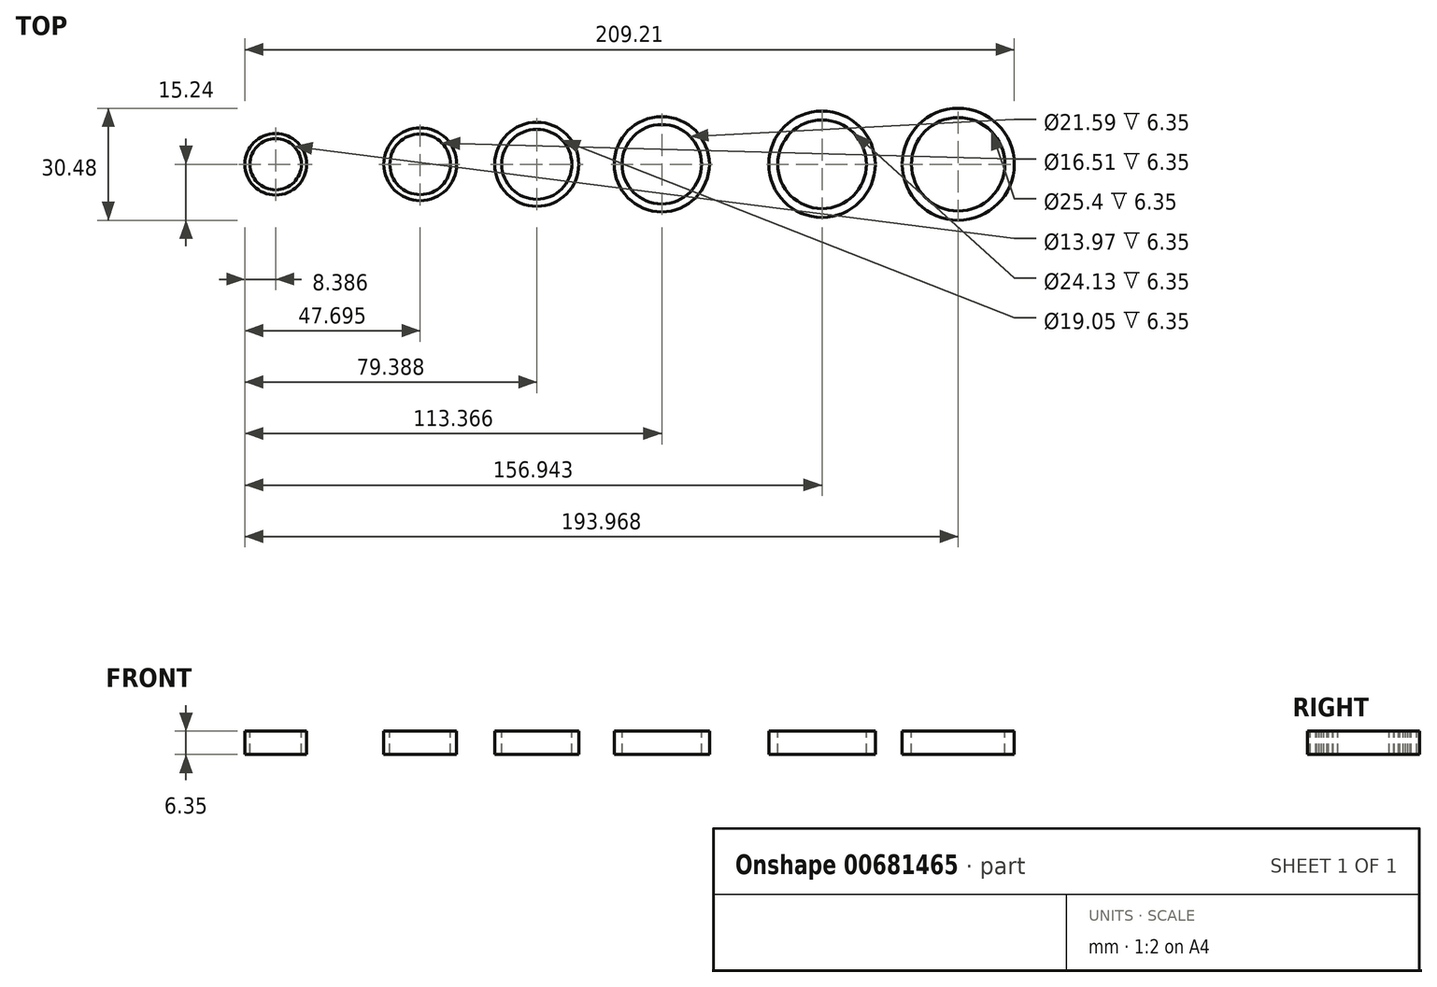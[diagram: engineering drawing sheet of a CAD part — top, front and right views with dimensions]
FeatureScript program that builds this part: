
annotation { "Feature Type Name" : "Feature", "Feature Type Description" : "" }
export const myFeature = defineFeature(function(context is Context, id is Id, definition is map)
    precondition{}
    {
        {
            var Q0;
            Q0=qCreatedBy(makeId("Top.planeOp"),FACE);
            var sketch = newSketch(context, id + "F0", { "sketchPlane" : qUnion([Q0])});
            skLineSegment(sketch, "E0", {"start": v(-152.37, 0) * mm, "end": v(157.04, 0) * mm, "construction": true});
            skCircle(sketch, "E1", {"center": v(-138.06, 0) * mm, "radius": 6.99 * mm});
            skCircle(sketch, "E2", {"center": v(-138.06, 0) * mm, "radius": 8.38 * mm});
            skCircle(sketch, "E3", {"center": v(-98.75, 0) * mm, "radius": 8.26 * mm});
            skCircle(sketch, "E4", {"center": v(-98.75, 0) * mm, "radius": 9.9 * mm});
            skCircle(sketch, "E5", {"center": v(-67.06, 0) * mm, "radius": 9.53 * mm});
            skCircle(sketch, "E6", {"center": v(-33.08, 0) * mm, "radius": 10.8 * mm});
            skCircle(sketch, "E7", {"center": v(10.5, 0) * mm, "radius": 12.07 * mm});
            skCircle(sketch, "E8", {"center": v(47.52, 0) * mm, "radius": 12.7 * mm});
            skCircle(sketch, "E9", {"center": v(-67.06, 0) * mm, "radius": 11.43 * mm});
            skCircle(sketch, "E10", {"center": v(-33.08, 0) * mm, "radius": 12.95 * mm});
            skCircle(sketch, "E11", {"center": v(10.5, 0) * mm, "radius": 14.48 * mm});
            skCircle(sketch, "E12", {"center": v(47.52, 0) * mm, "radius": 15.24 * mm});
            skSolve(sketch);
        }
        {
            var Q0;
            Q0 = qSketchRegion(id + "F0", true);
            extrude(context, id + "F1", {"entities" : qUnion([Q0]), "oppositeDirection" : true, "depth" : 6.35 * mm, "offsetDistance" : 25.4 * mm});
        }
    });
